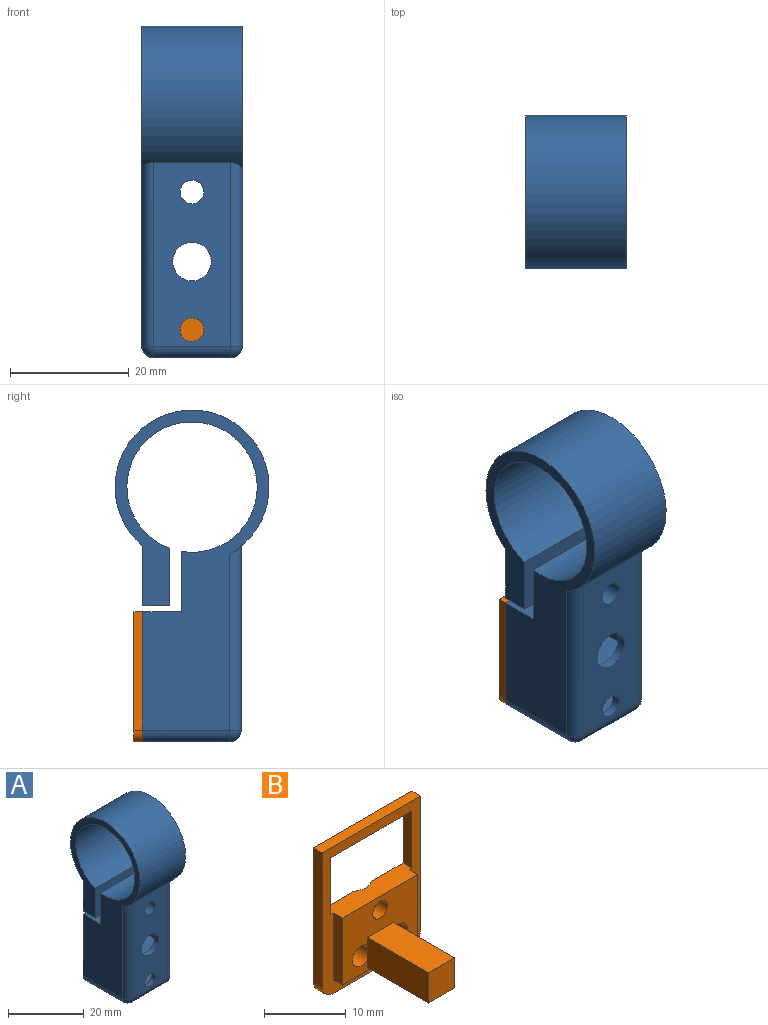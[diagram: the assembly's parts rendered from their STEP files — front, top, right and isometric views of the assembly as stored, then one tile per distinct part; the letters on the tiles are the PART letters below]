
ASSEMBLY  parts=2 mates=1
PART A: 43 faces, bbox 17x26x56 mm
  f0: plane 15.11x10.5mm, normal (-1,0,0), area 104.2mm2, adj f1,f18,f26,f27,f33,f34
  f1: plane 14x6.5mm, normal (0,1,0), area 78.4mm2, adj f0,f17,f26,f31,f34
  f2: plane 14x8.5mm, normal (0,1,0), area 85.8mm2, adj f20,f27,f28,f29,f30
  f3: plane 17x10mm, normal (0,1,0), area 121.2mm2, adj f5,f6,f7,f8,f9,f10,f11,f12
  f4: cylinder r=2mm len=4mm, axis (0,-1,0), area 19.3mm2, adj f21,f22
  f5: plane 4.33x3mm, normal (0,0,1), area 13mm2, adj f3,f6,f10,f21
  f6: plane 3.75x3mm, normal (0.87,0,0.5), area 13mm2, adj f3,f5,f7,f21
  f7: plane 3.75x3mm, normal (0.87,0,-0.5), area 13mm2, adj f3,f6,f8,f21
  f8: plane 4.33x3mm, normal (0,0,-1), area 13mm2, adj f3,f7,f9,f21
  f9: plane 3.75x3mm, normal (-0.87,0,-0.5), area 13mm2, adj f3,f8,f10,f21
  f10: plane 3.75x3mm, normal (-0.87,0,0.5), area 13mm2, adj f3,f5,f9,f21
  f11: cylinder r=13mm len=26mm, axis (-1,0,0), area 1084.1mm2, adj f3,f12,f13,f19,f37,f38
  f12: plane 54x26mm, normal (1,0,0), area 545.9mm2, adj f3,f11,f14,f18,f22,f23,f24,f25
  f13: plane 54x26mm, normal (-1,0,0), area 545.9mm2, adj f3,f11,f14,f18,f22,f23,f24,f25
  f14: cylinder r=11mm len=22mm, axis (-1,0,0), area 1139.5mm2, adj f12,f13,f22,f25
  f15: plane 14.61x13mm, normal (0,0,-1), area 189.9mm2, adj f18,f36,f39,f42
  f16: cylinder r=2mm len=10.08mm, axis (0,-1,0), area 126.6mm2, adj f19,f25
  f17: cylinder r=2mm len=4mm, axis (0,-1,0), area 18.8mm2, adj f1,f19
  f18: plane 22x17mm, normal (0,1,0), area 106.2mm2, adj f0,f12,f13,f15,f24,f26,f27,f28
  f19: plane 31x13mm, normal (0,-1,0), area 344.6mm2, adj f11,f16,f17,f20,f37,f38,f42
  f20: cylinder r=3.25mm len=6.5mm, axis (0,-1,0), area 30.6mm2, adj f2,f19
  f21: plane 8.66x7.5mm, normal (0,1,0), area 36.1mm2, adj f4,f5,f6,f7,f8,f9,f10
  f22: plane 17x9.67mm, normal (0,-1,0), area 151.7mm2, adj f4,f12,f13,f14,f23
  f23: plane 17x4.54mm, normal (0,0,-1), area 77.1mm2, adj f3,f12,f13,f22
  f24: plane 17x6.54mm, normal (0,0,1), area 111.1mm2, adj f12,f13,f18,f25
  f25: plane 17x10.14mm, normal (0,1,0), area 159.8mm2, adj f12,f13,f14,f16,f24
  f26: plane 15.11x14mm, normal (0,0,1), area 211.5mm2, adj f0,f1,f18,f31
  f27: plane 15.11x14mm, normal (0,0,1), area 190.6mm2, adj f0,f2,f18,f28,f30,f31,f33
  f28: plane 15.11x8.5mm, normal (-1,0,0), area 128.5mm2, adj f2,f18,f27,f29
  f29: plane 15.11x14mm, normal (0,0,-1), area 211.6mm2, adj f2,f18,f28,f30
  f30: plane 15.11x8.5mm, normal (1,0,0), area 128.5mm2, adj f2,f18,f27,f29
  f31: plane 15.11x10.5mm, normal (1,0,0), area 104.2mm2, adj f1,f18,f26,f27,f33,f34
  f32: cylinder r=1.25mm len=13.61mm, axis (0,-1,0), area 106.9mm2, adj f33,f35
  f33: plane 14x4mm, normal (0,1,0), area 51.1mm2, adj f0,f27,f31,f32,f34
  f34: plane 14x13.61mm, normal (0,0,-1), area 190.5mm2, adj f0,f1,f31,f33
  f35: plane 2.5x2.5mm, normal (0,1,0), area 4.9mm2, adj f32
  f36: cylinder r=2mm len=14.61mm, axis (0,-1,0), area 45.9mm2, adj f13,f15,f18,f40
  f37: cylinder r=2mm len=31mm, axis (0,0,-1), area 95.7mm2, adj f11,f13,f19,f40
  f38: cylinder r=2mm len=31mm, axis (0,0,1), area 95.7mm2, adj f11,f12,f19,f41
  f39: cylinder r=2mm len=14.61mm, axis (0,1,0), area 45.9mm2, adj f12,f15,f18,f41
  f40: sphere r=2mm, area 6.3mm2, adj f36,f37,f42
  f41: sphere r=2mm, area 6.3mm2, adj f38,f39,f42
  f42: cylinder r=2mm len=13mm, axis (1,0,0), area 40.8mm2, adj f15,f19,f40,f41
PART B: 27 faces, bbox 17x13.6x22 mm
  f0: plane 2.24x0.5mm, normal (0,1,0), area 0.8mm2, adj f19,f25
  f1: plane 2.24x0.5mm, normal (0,1,0), area 0.8mm2, adj f18,f24
  f2: plane 14x3mm, normal (0,0,1), area 39.5mm2, adj f3,f5,f6,f7,f11,f13,f15,f16
  f3: plane 13x10mm, normal (0,-1,0), area 92.2mm2, adj f2,f4,f5,f6,f17,f18,f19,f22
  f4: plane 13x1.5mm, normal (0,0,-1), area 19.5mm2, adj f3,f5,f6,f7
  f5: plane 10x1.5mm, normal (-1,0,0), area 15mm2, adj f2,f3,f4,f7
  f6: plane 10x1.5mm, normal (1,0,0), area 15mm2, adj f2,f3,f4,f7
  f7: plane 22x17mm, normal (0,-1,0), area 123.2mm2, adj f2,f4,f5,f6,f8,f9,f10,f11
  f8: plane 20x1.5mm, normal (1,0,0), area 30mm2, adj f7,f9,f15,f21
  f9: plane 17x1.5mm, normal (0,0,1), area 25.5mm2, adj f7,f8,f10,f15
  f10: plane 20x1.5mm, normal (-1,0,0), area 30mm2, adj f7,f9,f15,f20
  f11: plane 8.5x1.5mm, normal (1,0,0), area 12.7mm2, adj f2,f7,f12,f15
  f12: plane 14x1.5mm, normal (0,0,-1), area 21mm2, adj f7,f11,f13,f15
  f13: plane 8.5x1.5mm, normal (-1,0,0), area 12.7mm2, adj f2,f7,f12,f15
  f14: plane 13x1.5mm, normal (0,0,-1), area 19.5mm2, adj f7,f15,f20,f21
  f15: plane 22x17mm, normal (0,1,0), area 220.4mm2, adj f2,f8,f9,f10,f11,f12,f13,f14
  f16: cone r=1.25mm half-angle=45deg, axis (0,1,0), area 19.4mm2, adj f2,f15,f17
  f17: cylinder r=1.25mm len=2.5mm, axis (0,-1,0), area 13.7mm2, adj f3,f16
  f18: cylinder r=1.5mm len=3mm, axis (0,1,0), area 28.3mm2, adj f1,f3,f15
  f19: cylinder r=1.5mm len=3mm, axis (0,1,0), area 28.3mm2, adj f0,f3,f15
  f20: cylinder r=2mm len=2mm, axis (0,-1,0), area 4.7mm2, adj f7,f10,f14,f15
  f21: cylinder r=2mm len=2mm, axis (0,1,0), area 4.7mm2, adj f7,f8,f14,f15
  f22: plane 10.61x4.5mm, normal (0,0,-1), area 47.8mm2, adj f3,f24,f25,f26
  f23: plane 10.61x4.5mm, normal (0,0,1), area 47.8mm2, adj f3,f24,f25,f26
  f24: plane 10.61x4.5mm, normal (-1,0,0), area 47.8mm2, adj f1,f3,f22,f23,f26
  f25: plane 10.61x4.5mm, normal (1,0,0), area 47.8mm2, adj f0,f3,f22,f23,f26
  f26: plane 4.5x4.5mm, normal (0,-1,0), area 20.2mm2, adj f22,f23,f24,f25
PLACE A t=(-6.44,14.66,25.44)mm
PLACE B t=(-6.44,14.66,25.44)mm
MATE fastened A.f32 <-> B.f16  axis (0,1,0) through (-6.44,21.47,16.38)mm
